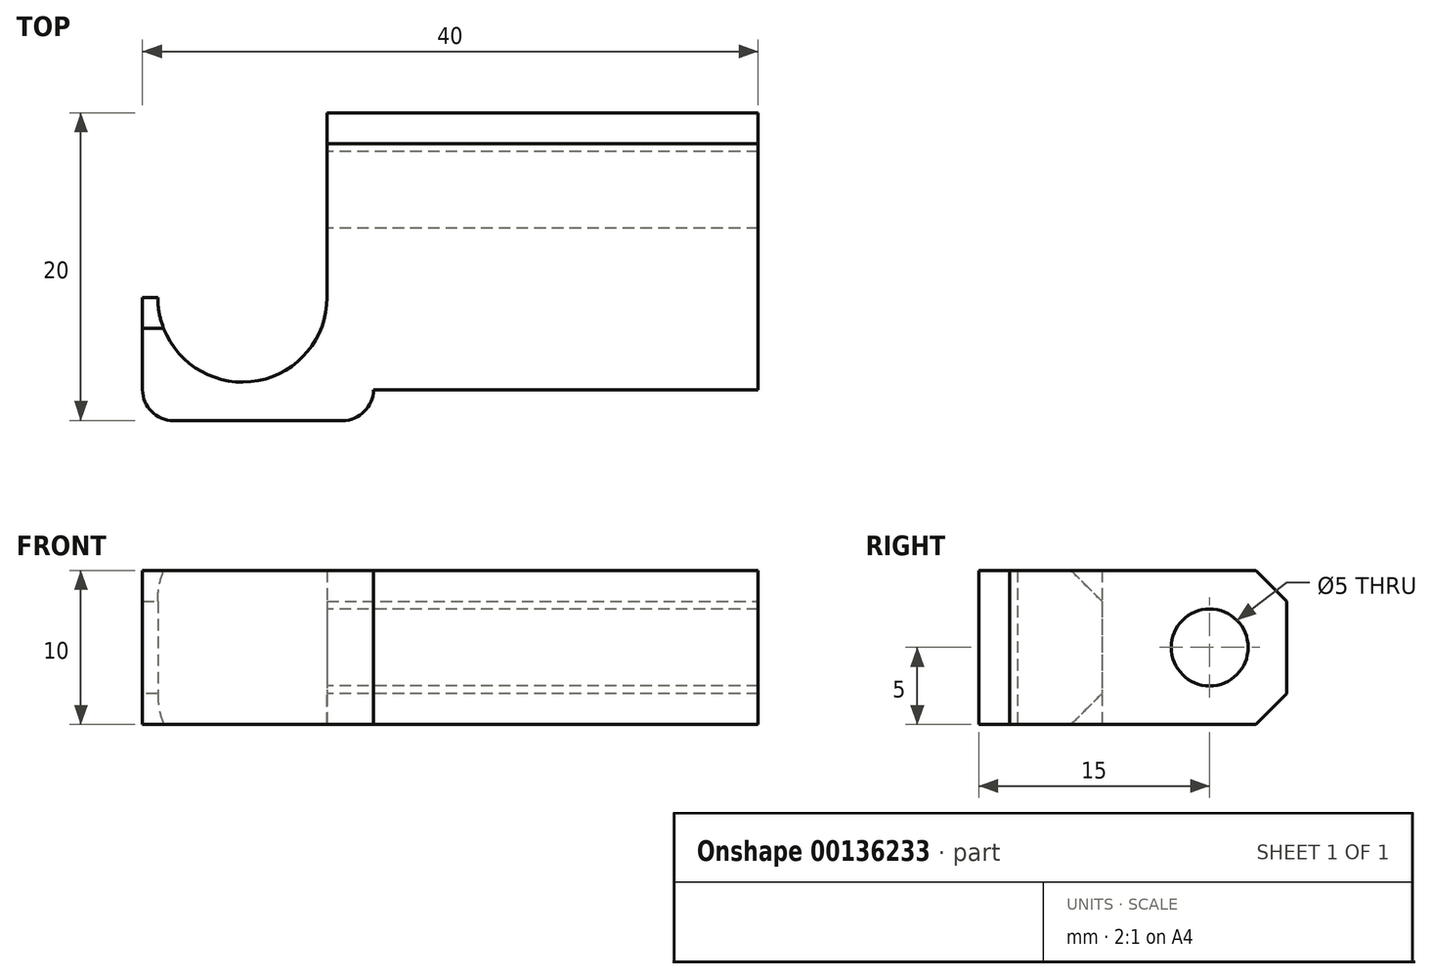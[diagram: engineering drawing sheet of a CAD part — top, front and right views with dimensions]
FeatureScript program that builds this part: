
annotation { "Feature Type Name" : "Feature", "Feature Type Description" : "" }
export const myFeature = defineFeature(function(context is Context, id is Id, definition is map)
    precondition{}
    {
        {
            var Q0;
            Q0=qCreatedBy(makeId("Top.planeOp"),FACE);
            var sketch = newSketch(context, id + "F0", { "sketchPlane" : qUnion([Q0])});
            skLineSegment(sketch, "E0", {"start": v(0, 2) * mm, "end": v(0, 20) * mm});
            skLineSegment(sketch, "E1", {"start": v(0, 20) * mm, "end": v(-3, 20) * mm});
            skLineSegment(sketch, "E2", {"start": v(-3, 20) * mm, "end": v(-3, 8) * mm});
            skLineSegment(sketch, "E3", {"start": v(-3, 8) * mm, "end": v(-3, 8) * mm});
            skLineSegment(sketch, "E4", {"start": v(-15, 8) * mm, "end": v(-15, 2) * mm});
            skLineSegment(sketch, "E5", {"start": v(-2, 0) * mm, "end": v(-13, 0) * mm});
            skArc(sketch, "E6", {"start": v(-14, 8) * mm, "mid": v(-8.5, 2.5) * mm, "end": v(-3, 8) * mm});
            skPoint(sketch, "E7.visualSharp", {"position": v(0, 0) * mm});
            skArc(sketch, "E7.filletArc", {"start": v(-2, 0) * mm, "mid": v(-0.59, 0.59) * mm, "end": v(0, 2) * mm});
            skPoint(sketch, "E8.visualSharp", {"position": v(-15, 0) * mm});
            skArc(sketch, "E8.filletArc", {"start": v(-15, 2) * mm, "mid": v(-14.41, 0.59) * mm, "end": v(-13, 0) * mm});
            skLineSegment(sketch, "E9.trimOffspring", {"start": v(-14, 8) * mm, "end": v(-15, 8) * mm});
            skSolve(sketch);
        }
        {
            var Q0;
            Q0=makeQuery(id+"F0.imprint","IMPRINT",FACE,{"disambiguationData":[TD([[makeQuery(id+"F0.imprint","IMPRINT",EDGE,{"derivedFrom":sQuery(id+"F0.wireOp",EDGE,"E0")}),1.0]])]});
            extrude(context, id + "F1", {"entities" : qUnion([Q0]), "depth" : 10 * mm});
        }
        {
            var Q0;
            Q0=makeQuery(id+"F1.opExtrude","CAP_EDGE",EDGE,{"disambiguationData":[OSD([sQuery(id+"F0.wireOp",EDGE,"E9.trimOffspring")])],"isStart":false});
            var Q1;
            Q1=makeQuery(id+"F1.opExtrude","CAP_EDGE",EDGE,{"disambiguationData":[OSD([sQuery(id+"F0.wireOp",EDGE,"E9.trimOffspring")])],"isStart":true});
            var Q2;
            Q2=makeQuery(id+"F1.opExtrude","CAP_EDGE",EDGE,{"disambiguationData":[OSD([sQuery(id+"F0.wireOp",EDGE,"E1")])],"isStart":false});
            var Q3;
            Q3=makeQuery(id+"F1.opExtrude","CAP_EDGE",EDGE,{"disambiguationData":[OSD([sQuery(id+"F0.wireOp",EDGE,"E1")])],"isStart":true});
            chamfer(context, id + "F2", {"entities" : qUnion([Q0, Q1, Q2, Q3]), "width" : 2 * mm, "tangentPropagation" : true});
        }
        {
            var Q0;
            Q0=makeQuery(id+"F1.opExtrude","SWEPT_FACE",FACE,{"disambiguationData":[OSD([sQuery(id+"F0.wireOp",EDGE,"E2")])]});
            var sketch = newSketch(context, id + "F3", { "sketchPlane" : qUnion([Q0])});
            skCircle(sketch, "E10", {"center": v(-15, 5) * mm, "radius": 2.5 * mm});
            skSolve(sketch);
        }
        {
            var Q0;
            Q0=makeQuery(id+"F3.imprint","IMPRINT",FACE,{"disambiguationData":[TD([[makeQuery(id+"F3.imprint","IMPRINT",EDGE,{"derivedFrom":sQuery(id+"F3.wireOp",EDGE,"E10")}),1.0]])]});
            extrude(context, id + "F4", {"entities" : qUnion([Q0]), "operationType" : NewBodyOperationType.REMOVE, "oppositeDirection" : true, "depth" : 25 * mm});
        }
        {
            var Q0;
            Q0=makeQuery(id+"F1.opExtrude","SWEPT_FACE",FACE,{"disambiguationData":[OSD([sQuery(id+"F0.wireOp",EDGE,"E0")])]});
            extrude(context, id + "F5", {"entities" : qUnion([Q0]), "operationType" : NewBodyOperationType.ADD, "depth" : 25 * mm});
        }
    });
